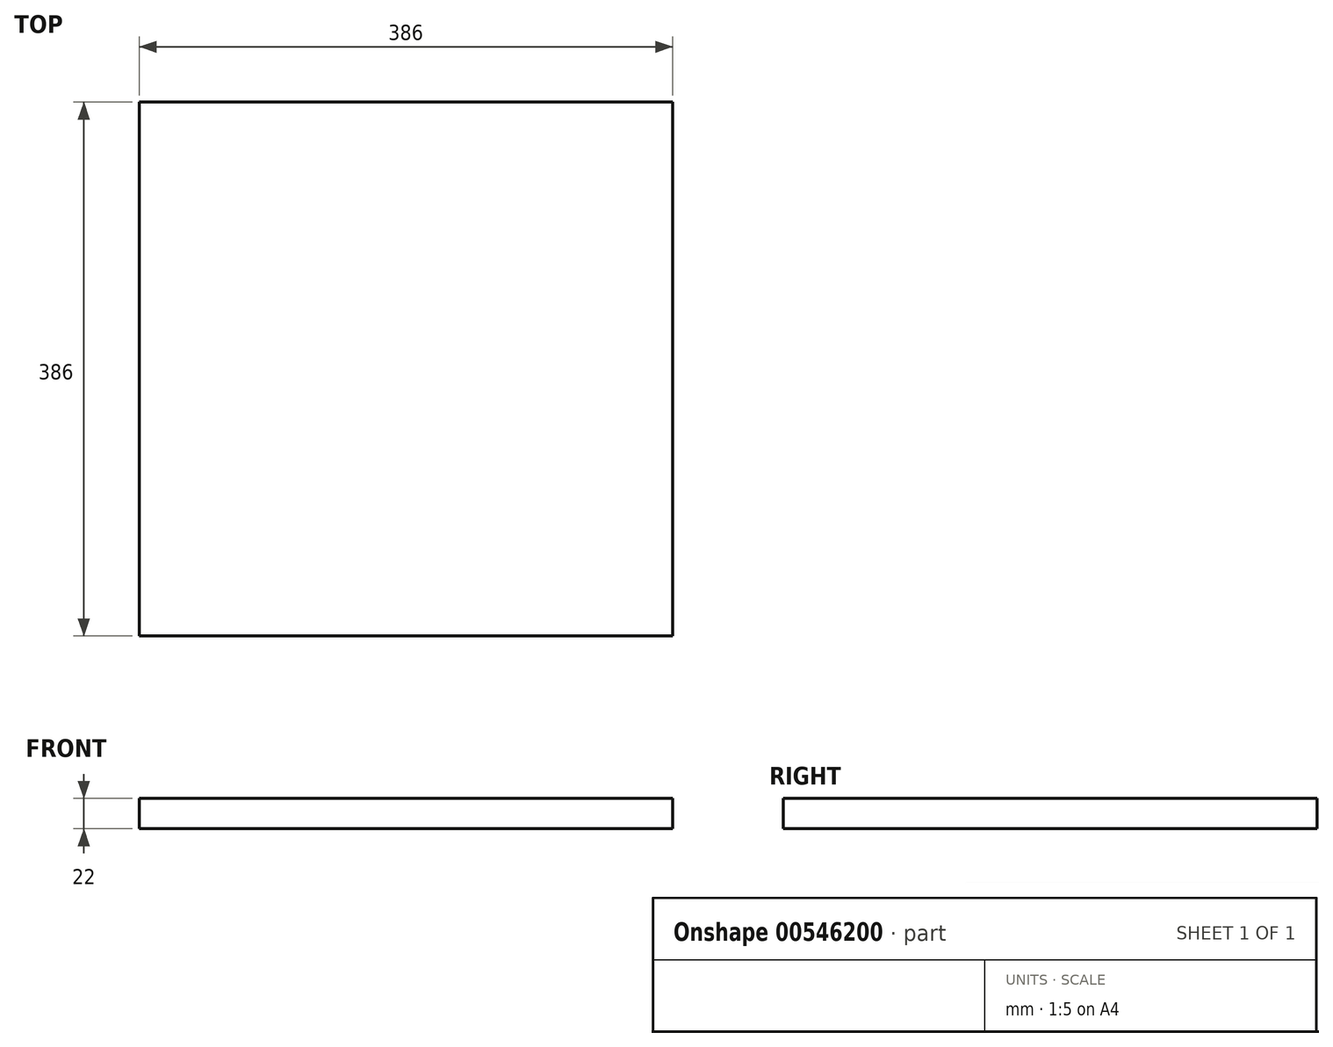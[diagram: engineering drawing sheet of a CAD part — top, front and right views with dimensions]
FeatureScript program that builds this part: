
annotation { "Feature Type Name" : "Feature", "Feature Type Description" : "" }
export const myFeature = defineFeature(function(context is Context, id is Id, definition is map)
    precondition{}
    {
        {
            var Q0;
            Q0=qCreatedBy(makeId("Top.planeOp"),FACE);
            var sketch = newSketch(context, id + "F0", { "sketchPlane" : qUnion([Q0])});
            skLineSegment(sketch, "E0.bottom", {"start": v(0, 0) * mm, "end": v(386, 0) * mm});
            skLineSegment(sketch, "E0.top", {"start": v(0, 386) * mm, "end": v(386, 386) * mm});
            skLineSegment(sketch, "E0.left", {"start": v(0, 0) * mm, "end": v(0, 386) * mm});
            skLineSegment(sketch, "E0.right", {"start": v(386, 0) * mm, "end": v(386, 386) * mm});
            skSolve(sketch);
        }
        {
            var Q0;
            Q0 = qSketchRegion(id + "F0", true);
            extrude(context, id + "F1", {"entities" : qUnion([Q0]), "depth" : 22 * mm, "offsetDistance" : 25 * mm});
        }
    });
